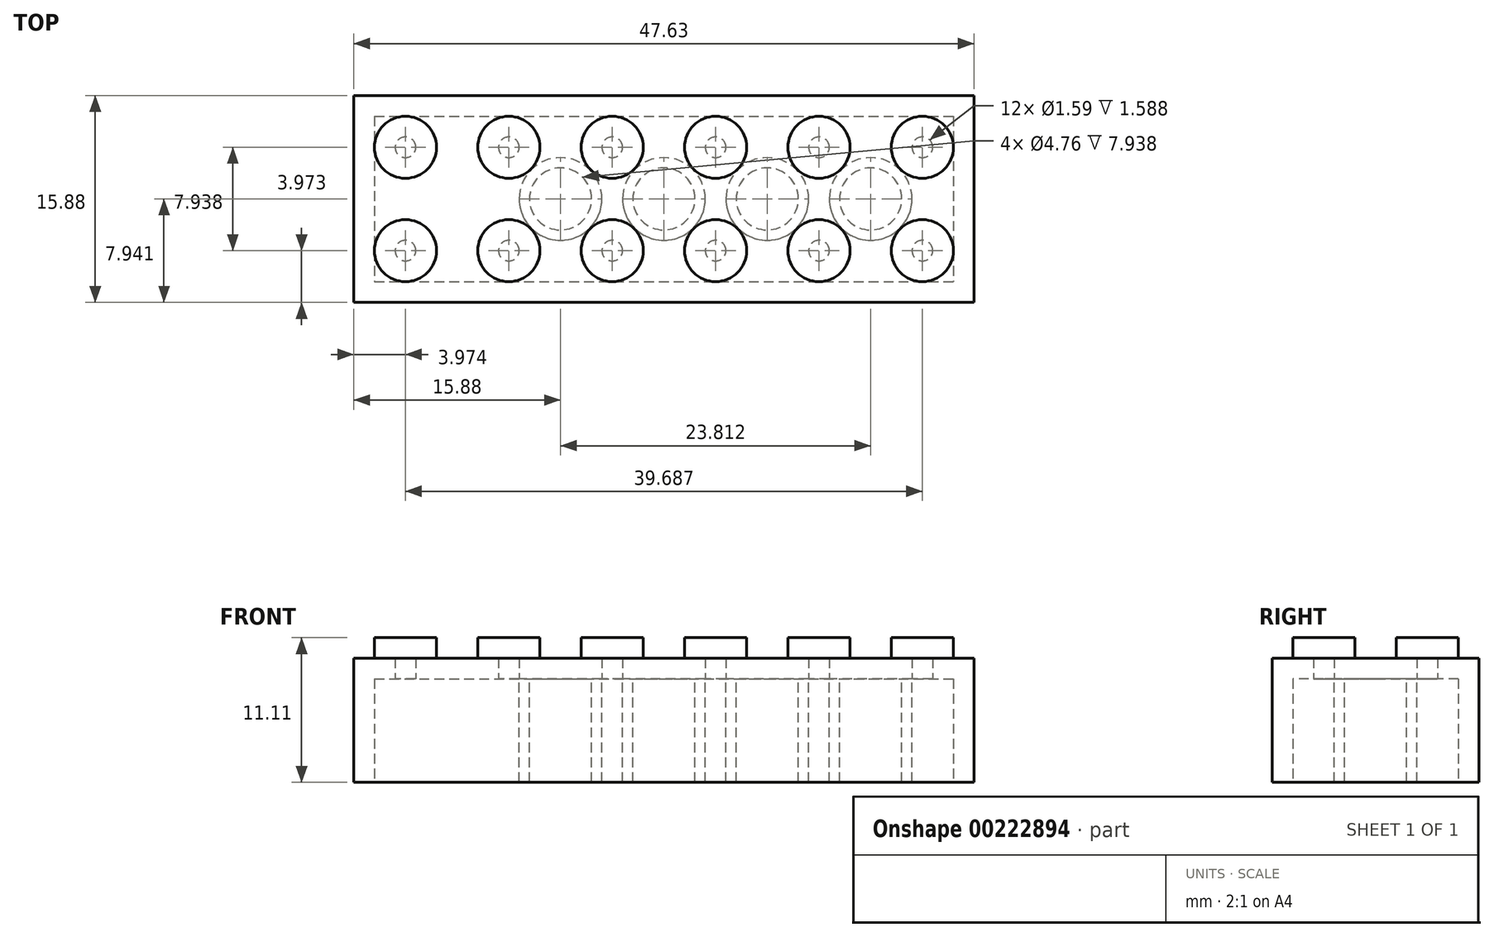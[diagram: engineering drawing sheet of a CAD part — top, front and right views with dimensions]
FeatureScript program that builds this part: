
annotation { "Feature Type Name" : "Feature", "Feature Type Description" : "" }
export const myFeature = defineFeature(function(context is Context, id is Id, definition is map)
    precondition{}
    {
        {
            var Q0;
            Q0=qCreatedBy(makeId("Top.planeOp"),FACE);
            var sketch = newSketch(context, id + "F0", { "sketchPlane" : qUnion([Q0])});
            skLineSegment(sketch, "E0.bottom", {"start": v(-15.88, 3.97) * mm, "end": v(31.75, 3.97) * mm});
            skLineSegment(sketch, "E0.top", {"start": v(-15.88, -11.9) * mm, "end": v(31.75, -11.9) * mm});
            skLineSegment(sketch, "E0.left", {"start": v(-15.88, 3.97) * mm, "end": v(-15.88, -11.9) * mm});
            skLineSegment(sketch, "E0.right", {"start": v(31.75, 3.97) * mm, "end": v(31.75, -11.9) * mm});
            skCircle(sketch, "E1", {"center": v(-11.9, 0) * mm, "radius": 2.38 * mm});
            skCircle(sketch, "E2.0.1.0", {"center": v(-11.9, -7.94) * mm, "radius": 2.38 * mm});
            skCircle(sketch, "E2.1.0.0", {"center": v(-3.97, 0) * mm, "radius": 2.38 * mm});
            skCircle(sketch, "E2.1.1.0", {"center": v(-3.97, -7.94) * mm, "radius": 2.38 * mm});
            skCircle(sketch, "E2.2.0.0", {"center": v(3.97, 0) * mm, "radius": 2.38 * mm});
            skCircle(sketch, "E2.2.1.0", {"center": v(3.97, -7.94) * mm, "radius": 2.38 * mm});
            skCircle(sketch, "E2.3.0.0", {"center": v(11.9, 0) * mm, "radius": 2.38 * mm});
            skCircle(sketch, "E2.3.1.0", {"center": v(11.9, -7.94) * mm, "radius": 2.38 * mm});
            skLineSegment(sketch, "E2.direction1", {"start": v(-11.9, 0) * mm, "end": v(-3.97, 0) * mm, "construction": true});
            skLineSegment(sketch, "E2.direction2", {"start": v(-11.9, 0) * mm, "end": v(-11.9, -7.94) * mm, "construction": true});
            skCircle(sketch, "E3.0.4.0", {"center": v(19.84, 0) * mm, "radius": 2.38 * mm});
            skCircle(sketch, "E3.0.4.1", {"center": v(19.84, -7.94) * mm, "radius": 2.38 * mm});
            skCircle(sketch, "E3.0.5.0", {"center": v(27.78, 0) * mm, "radius": 2.38 * mm});
            skCircle(sketch, "E3.0.5.1", {"center": v(27.78, -7.94) * mm, "radius": 2.38 * mm});
            skSolve(sketch);
        }
        {
            var Q0;
            Q0=makeQuery(id+"F0.imprint","IMPRINT",FACE,{"disambiguationData":[TD([[makeQuery(id+"F0.imprint","IMPRINT",EDGE,{"derivedFrom":sQuery(id+"F0.wireOp",EDGE,"E0.bottom")}),-1.0]])]});
            extrude(context, id + "F1", {"entities" : qUnion([Q0]), "depth" : 9.52 * mm});
        }
        {
            var Q0;
            Q0=makeQuery(id+"F0.imprint","IMPRINT",FACE,{"disambiguationData":[TD([[makeQuery(id+"F0.imprint","IMPRINT",EDGE,{"derivedFrom":sQuery(id+"F0.wireOp",EDGE,"E1")}),1.0]])]});
            var Q1;
            Q1=makeQuery(id+"F0.imprint","IMPRINT",FACE,{"disambiguationData":[TD([[makeQuery(id+"F0.imprint","IMPRINT",EDGE,{"derivedFrom":sQuery(id+"F0.wireOp",EDGE,"E2.0.1.0")}),1.0]])]});
            var Q2;
            Q2=makeQuery(id+"F0.imprint","IMPRINT",FACE,{"disambiguationData":[TD([[makeQuery(id+"F0.imprint","IMPRINT",EDGE,{"derivedFrom":sQuery(id+"F0.wireOp",EDGE,"E2.1.1.0")}),1.0]])]});
            var Q3;
            Q3=makeQuery(id+"F0.imprint","IMPRINT",FACE,{"disambiguationData":[TD([[makeQuery(id+"F0.imprint","IMPRINT",EDGE,{"derivedFrom":sQuery(id+"F0.wireOp",EDGE,"E2.1.0.0")}),1.0]])]});
            var Q4;
            Q4=makeQuery(id+"F0.imprint","IMPRINT",FACE,{"disambiguationData":[TD([[makeQuery(id+"F0.imprint","IMPRINT",EDGE,{"derivedFrom":sQuery(id+"F0.wireOp",EDGE,"E2.2.0.0")}),1.0]])]});
            var Q5;
            Q5=makeQuery(id+"F0.imprint","IMPRINT",FACE,{"disambiguationData":[TD([[makeQuery(id+"F0.imprint","IMPRINT",EDGE,{"derivedFrom":sQuery(id+"F0.wireOp",EDGE,"E2.2.1.0")}),1.0]])]});
            var Q6;
            Q6=makeQuery(id+"F0.imprint","IMPRINT",FACE,{"disambiguationData":[TD([[makeQuery(id+"F0.imprint","IMPRINT",EDGE,{"derivedFrom":sQuery(id+"F0.wireOp",EDGE,"E2.3.1.0")}),1.0]])]});
            var Q7;
            Q7=makeQuery(id+"F0.imprint","IMPRINT",FACE,{"disambiguationData":[TD([[makeQuery(id+"F0.imprint","IMPRINT",EDGE,{"derivedFrom":sQuery(id+"F0.wireOp",EDGE,"E2.3.0.0")}),1.0]])]});
            var Q8;
            Q8=makeQuery(id+"F0.imprint","IMPRINT",FACE,{"disambiguationData":[TD([[makeQuery(id+"F0.imprint","IMPRINT",EDGE,{"derivedFrom":sQuery(id+"F0.wireOp",EDGE,"E3.0.4.0")}),1.0]])]});
            var Q9;
            Q9=makeQuery(id+"F0.imprint","IMPRINT",FACE,{"disambiguationData":[TD([[makeQuery(id+"F0.imprint","IMPRINT",EDGE,{"derivedFrom":sQuery(id+"F0.wireOp",EDGE,"E3.0.5.0")}),1.0]])]});
            var Q10;
            Q10=makeQuery(id+"F0.imprint","IMPRINT",FACE,{"disambiguationData":[TD([[makeQuery(id+"F0.imprint","IMPRINT",EDGE,{"derivedFrom":sQuery(id+"F0.wireOp",EDGE,"E3.0.5.1")}),1.0]])]});
            var Q11;
            Q11=makeQuery(id+"F0.imprint","IMPRINT",FACE,{"disambiguationData":[TD([[makeQuery(id+"F0.imprint","IMPRINT",EDGE,{"derivedFrom":sQuery(id+"F0.wireOp",EDGE,"E3.0.4.1")}),1.0]])]});
            extrude(context, id + "F2", {"entities" : qUnion([Q0, Q1, Q2, Q3, Q4, Q5, Q6, Q7, Q8, Q9, Q10, Q11]), "operationType" : NewBodyOperationType.ADD, "depth" : 11.1 * mm});
        }
        {
            var Q0;
            {var subQ0=sQuery(id+"F0.wireOp",EDGE,"8b71ed98-f0e1-4300-85cb-82ad82c44b3e0.MirrorC");var subQ1=sQuery(id+"F0.wireOp",EDGE,"E1");Q0=makeQuery(id+"F2.boolean.opBoolean","MERGE",FACE,{"derivedFrom":[makeQuery(id+"F1.opExtrude","CAP_FACE",FACE,{"disambiguationData":[OSD([sQuery(id+"F0.wireOp",EDGE,"E0.bottom"),sQuery(id+"F0.wireOp",EDGE,"E0.top"),sQuery(id+"F0.wireOp",EDGE,"E0.left"),sQuery(id+"F0.wireOp",EDGE,"E0.right"),subQ1,subQ0])],"isStart":true}),makeQuery(id+"F2.opExtrude","CAP_FACE",FACE,{"disambiguationData":[OSD([subQ1])],"isStart":true}),makeQuery(id+"F2.opExtrude","CAP_FACE",FACE,{"disambiguationData":[OSD([subQ0])],"isStart":true})]});}
            shell(context, id + "F3", {"entities" : qUnion([Q0]), "thickness" : 1.59 * mm});
        }
        {
            var Q0;
            Q0=makeQuery(id+"F3.opShell","OFFSET_FACE",FACE,{"disambiguationData":[OSD([sQuery(id+"F0.wireOp",EDGE,"E0.bottom"),sQuery(id+"F0.wireOp",EDGE,"E0.top"),sQuery(id+"F0.wireOp",EDGE,"E0.left"),sQuery(id+"F0.wireOp",EDGE,"E0.right"),sQuery(id+"F0.wireOp",EDGE,"E1"),sQuery(id+"F0.wireOp",EDGE,"E2.0.1.0"),sQuery(id+"F0.wireOp",EDGE,"E2.1.0.0"),sQuery(id+"F0.wireOp",EDGE,"E2.1.1.0"),sQuery(id+"F0.wireOp",EDGE,"E2.2.0.0"),sQuery(id+"F0.wireOp",EDGE,"E2.2.1.0"),sQuery(id+"F0.wireOp",EDGE,"E2.3.0.0"),sQuery(id+"F0.wireOp",EDGE,"E2.3.1.0")])]});
            var sketch = newSketch(context, id + "F4", { "sketchPlane" : qUnion([Q0])});
            skLineSegment(sketch, "E4", {"start": v(-11.9, 7.94) * mm, "end": v(-3.97, 0) * mm});
            skCircle(sketch, "E5", {"center": v(-7.94, 3.97) * mm, "radius": 3.18 * mm});
            skCircle(sketch, "E6.0", {"center": v(-7.94, 3.97) * mm, "radius": 2.38 * mm});
            skCircle(sketch, "E7.1.0.0", {"center": v(0, 3.97) * mm, "radius": 3.18 * mm});
            skCircle(sketch, "E7.1.0.1", {"center": v(0, 3.97) * mm, "radius": 2.38 * mm});
            skCircle(sketch, "E7.2.0.0", {"center": v(7.94, 3.97) * mm, "radius": 3.18 * mm});
            skCircle(sketch, "E7.2.0.1", {"center": v(7.94, 3.97) * mm, "radius": 2.38 * mm});
            skLineSegment(sketch, "E7.direction1", {"start": v(-7.94, 3.97) * mm, "end": v(0, 3.97) * mm, "construction": true});
            skCircle(sketch, "E8.0.3.0", {"center": v(15.88, 3.97) * mm, "radius": 3.18 * mm});
            skCircle(sketch, "E8.2.3.0", {"center": v(15.88, 3.97) * mm, "radius": 2.38 * mm});
            skCircle(sketch, "E8.0.4.0", {"center": v(23.81, 3.97) * mm, "radius": 3.18 * mm});
            skCircle(sketch, "E8.2.4.0", {"center": v(23.81, 3.97) * mm, "radius": 2.38 * mm});
            skSolve(sketch);
        }
        {
            var Q0;
            {var subQ0=sQuery(id+"F4.wireOp",EDGE,"E5");var subQ1=sQuery(id+"F4.wireOp",EDGE,"E4");var subQ2=makeQuery(id+"F4.imprint","INTERSECT",VERTEX,{"disambiguationData":[OD(0.0)],"derivedFrom":[subQ1,subQ0]});Q0=makeQuery(id+"F4.imprint","IMPRINT",FACE,{"disambiguationData":[TD([[makeQuery(id+"F4.imprint","IMPRINT",EDGE,{"disambiguationData":[TD([[subQ2,-1.0]])],"derivedFrom":subQ1}),1.0]])]});}
            var Q1;
            {var subQ0=sQuery(id+"F4.wireOp",EDGE,"E5");var subQ1=sQuery(id+"F4.wireOp",EDGE,"E4");var subQ2=makeQuery(id+"F4.imprint","INTERSECT",VERTEX,{"disambiguationData":[OD(0.0)],"derivedFrom":[subQ1,subQ0]});Q1=makeQuery(id+"F4.imprint","IMPRINT",FACE,{"disambiguationData":[TD([[makeQuery(id+"F4.imprint","IMPRINT",EDGE,{"disambiguationData":[TD([[subQ2,-1.0]])],"derivedFrom":subQ1}),-1.0]])]});}
            var Q2;
            Q2=makeQuery(id+"F4.imprint","IMPRINT",FACE,{"disambiguationData":[TD([[makeQuery(id+"F4.imprint","IMPRINT",EDGE,{"derivedFrom":sQuery(id+"F4.wireOp",EDGE,"E7.1.0.0")}),1.0]])]});
            var Q3;
            Q3=makeQuery(id+"F4.imprint","IMPRINT",FACE,{"disambiguationData":[TD([[makeQuery(id+"F4.imprint","IMPRINT",EDGE,{"derivedFrom":sQuery(id+"F4.wireOp",EDGE,"E7.2.0.0")}),1.0]])]});
            var Q4;
            Q4=makeQuery(id+"F4.imprint","IMPRINT",FACE,{"disambiguationData":[TD([[makeQuery(id+"F4.imprint","IMPRINT",EDGE,{"derivedFrom":sQuery(id+"F4.wireOp",EDGE,"E8.0.3.0")}),1.0]])]});
            var Q5;
            Q5=makeQuery(id+"F4.imprint","IMPRINT",FACE,{"disambiguationData":[TD([[makeQuery(id+"F4.imprint","IMPRINT",EDGE,{"derivedFrom":sQuery(id+"F4.wireOp",EDGE,"E8.0.4.0")}),1.0]])]});
            extrude(context, id + "F5", {"entities" : qUnion([Q0, Q1, Q2, Q3, Q4, Q5]), "operationType" : NewBodyOperationType.ADD, "depth" : 7.94 * mm});
        }
    });
